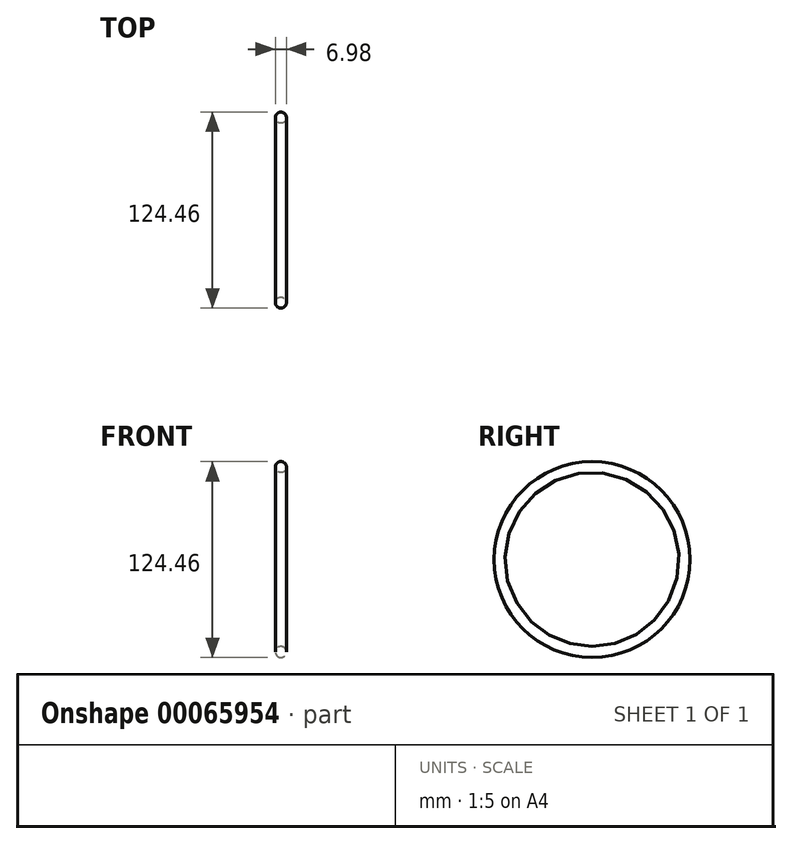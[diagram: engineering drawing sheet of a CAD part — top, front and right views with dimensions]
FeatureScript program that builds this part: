
annotation { "Feature Type Name" : "Feature", "Feature Type Description" : "" }
export const myFeature = defineFeature(function(context is Context, id is Id, definition is map)
    precondition{}
    {
        {
            var Q0;
            Q0=qCreatedBy(makeId("Front.planeOp"),FACE);
            var sketch = newSketch(context, id + "F0", { "sketchPlane" : qUnion([Q0])});
            skLineSegment(sketch, "E0", {"start": v(0, 0) * mm, "end": v(-6.06, 0) * mm, "construction": true});
            skCircle(sketch, "E1", {"center": v(0, 58.74) * mm, "radius": 3.5 * mm});
            skSolve(sketch);
        }
        {
            var Q0;
            Q0=makeQuery(id+"F0.imprint","IMPRINT",FACE,{"disambiguationData":[TD([[makeQuery(id+"F0.imprint","IMPRINT",EDGE,{"derivedFrom":sQuery(id+"F0.wireOp",EDGE,"E1")}),1.0]])]});
            var Q1;
            Q1=sQuery(id+"F0.wireOp",EDGE,"E0");
            revolve(context, id + "F1", {"entities" : qUnion([Q0]), "axis" : qUnion([Q1]), "revolveType" : RevolveType.FULL});
        }
    });
